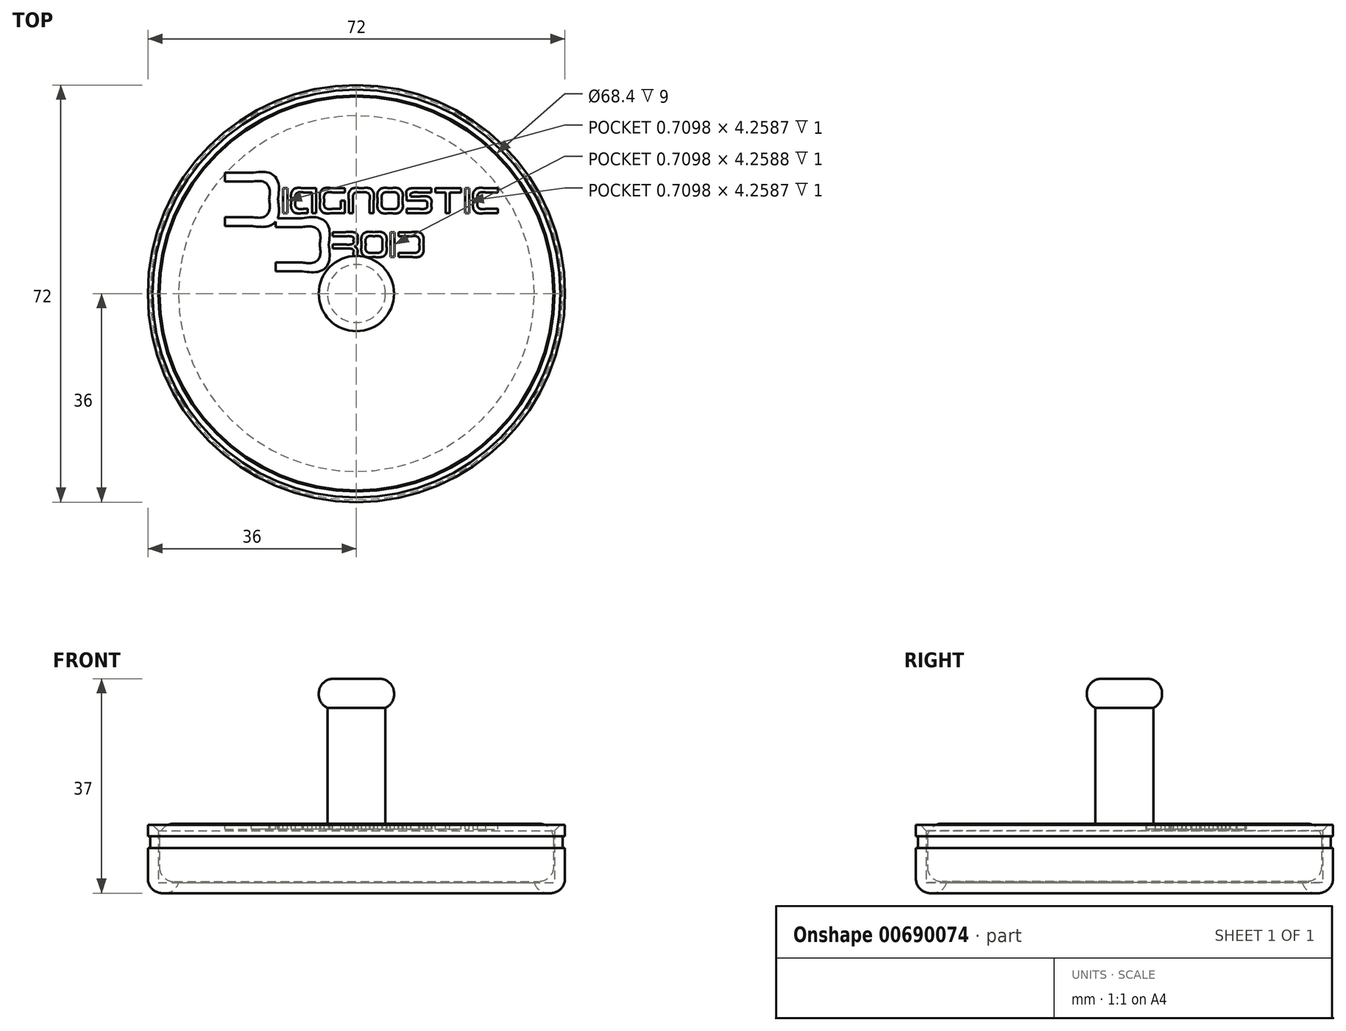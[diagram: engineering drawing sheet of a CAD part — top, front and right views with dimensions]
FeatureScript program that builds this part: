
annotation { "Feature Type Name" : "Feature", "Feature Type Description" : "" }
export const myFeature = defineFeature(function(context is Context, id is Id, definition is map)
    precondition{}
    {
        {
            var Q0;
            Q0=qCreatedBy(makeId("Front.planeOp"),FACE);
            var sketch = newSketch(context, id + "F0", { "sketchPlane" : qUnion([Q0])});
            skLineSegment(sketch, "E0.bottom", {"start": v(0, 0) * mm, "end": v(-34, 0) * mm});
            skLineSegment(sketch, "E0.top", {"start": v(0, 10) * mm, "end": v(-34, 10) * mm});
            skLineSegment(sketch, "E0.left", {"start": v(0, 0) * mm, "end": v(0, 10) * mm});
            skLineSegment(sketch, "E0.right", {"start": v(-34, 0) * mm, "end": v(-34, 6.5) * mm});
            skPoint(sketch, "E1.oppositeSnap0", {"position": v(-34, 5) * mm});
            skLineSegment(sketch, "E2.trimOffspring", {"start": v(-34, 3.5) * mm, "end": v(-34, 10) * mm});
            skLineSegment(sketch, "E3", {"start": v(-34, 6.5) * mm, "end": v(-34, 3.5) * mm});
            skPoint(sketch, "E1.top.end.orphan", {"position": v(-33.5, 6.5) * mm});
            skLineSegment(sketch, "E4.0", {"start": v(-36, -2) * mm, "end": v(-36, 9.8) * mm});
            skLineSegment(sketch, "E4.1", {"start": v(-30.7, -2) * mm, "end": v(-36, -2) * mm});
            skLineSegment(sketch, "E5.0", {"start": v(-34.2, -0.2) * mm, "end": v(-34.2, 9.8) * mm});
            skLineSegment(sketch, "E5.1", {"start": v(-30.7, -0.2) * mm, "end": v(-34.2, -0.2) * mm});
            skLineSegment(sketch, "E6", {"start": v(-34.2, 9.8) * mm, "end": v(-36, 9.8) * mm});
            skLineSegment(sketch, "E7", {"start": v(-30.7, -0.2) * mm, "end": v(-30.7, -2) * mm});
            skLineSegment(sketch, "E8.bottom", {"start": v(-36, 7.8) * mm, "end": v(-35.6, 7.8) * mm});
            skLineSegment(sketch, "E8.top", {"start": v(-36, 5.8) * mm, "end": v(-35.6, 5.8) * mm});
            skLineSegment(sketch, "E8.left", {"start": v(-36, 7.8) * mm, "end": v(-36, 5.8) * mm});
            skLineSegment(sketch, "E8.right", {"start": v(-35.6, 7.8) * mm, "end": v(-35.6, 5.8) * mm});
            skSolve(sketch);
        }
        {
            var Q0;
            Q0=makeQuery(id+"F0.imprint","IMPRINT",FACE,{"disambiguationData":[TD([[makeQuery(id+"F0.imprint","IMPRINT",EDGE,{"derivedFrom":sQuery(id+"F0.wireOp",EDGE,"E0.bottom")}),-1.0]])]});
            var Q1;
            Q1=makeQuery(id+"F0.imprint","IMPRINT",FACE,{"disambiguationData":[TD([[makeQuery(id+"F0.imprint","IMPRINT",EDGE,{"derivedFrom":sQuery(id+"F0.wireOp",EDGE,"E4.0")}),-1.0]])]});
            var Q2;
            Q2=sQuery(id+"F0.wireOp",EDGE,"E0.left");
            revolve(context, id + "F1", {"entities" : qUnion([Q0, Q1]), "axis" : qUnion([Q2]), "revolveType" : RevolveType.FULL});
        }
        {
            var Q0;
            Q0=makeQuery(id+"F1.opRevolve","SWEPT_FACE",FACE,{"disambiguationData":[OSD([sQuery(id+"F0.wireOp",EDGE,"E0.top")])]});
            var sketch = newSketch(context, id + "F2", { "sketchPlane" : qUnion([Q0])});
            skLineSegment(sketch, "E9", {"start": v(-11.94, 18.18) * mm, "end": v(-11.94, 13.92) * mm});
            skLineSegment(sketch, "E10", {"start": v(-11.94, 13.92) * mm, "end": v(-12.65, 13.92) * mm});
            skLineSegment(sketch, "E11", {"start": v(-12.65, 13.92) * mm, "end": v(-12.65, 18.18) * mm});
            skLineSegment(sketch, "E12", {"start": v(-12.65, 18.18) * mm, "end": v(-11.94, 18.18) * mm});
            skFitSpline(sketch, "E13", {"points": [v(-9.1, 17.47) * mm, v(-10.05, 17.47) * mm, v(-10.52, 17) * mm, v(-10.52, 16.05) * mm]});
            skFitSpline(sketch, "E14", {"points": [v(-10.52, 16.05) * mm, v(-10.52, 15.1) * mm, v(-10.05, 14.63) * mm, v(-9.1, 14.63) * mm]});
            skLineSegment(sketch, "E15", {"start": v(-6.97, 18.18) * mm, "end": v(-6.97, 13.92) * mm});
            skLineSegment(sketch, "E16", {"start": v(-6.97, 13.92) * mm, "end": v(-7.68, 13.92) * mm});
            skLineSegment(sketch, "E17", {"start": v(-7.68, 13.92) * mm, "end": v(-7.68, 17.47) * mm});
            skLineSegment(sketch, "E18", {"start": v(-7.68, 17.47) * mm, "end": v(-9.1, 17.47) * mm});
            skFitSpline(sketch, "E19", {"points": [v(-9.1, 13.92) * mm, v(-10.52, 13.92) * mm, v(-11.23, 14.63) * mm, v(-11.23, 16.05) * mm]});
            skFitSpline(sketch, "E20", {"points": [v(-11.23, 16.05) * mm, v(-11.23, 17.47) * mm, v(-10.52, 18.18) * mm, v(-9.1, 18.18) * mm]});
            skLineSegment(sketch, "E21", {"start": v(-9.1, 14.63) * mm, "end": v(-8.39, 14.63) * mm});
            skLineSegment(sketch, "E22", {"start": v(-8.39, 14.63) * mm, "end": v(-8.39, 13.92) * mm});
            skLineSegment(sketch, "E23", {"start": v(-8.39, 13.92) * mm, "end": v(-9.1, 13.92) * mm});
            skLineSegment(sketch, "E24", {"start": v(-9.1, 18.18) * mm, "end": v(-6.97, 18.18) * mm});
            skFitSpline(sketch, "E25", {"points": [v(-4.13, 13.92) * mm, v(-5.55, 13.92) * mm, v(-6.26, 14.63) * mm, v(-6.26, 16.05) * mm]});
            skFitSpline(sketch, "E26", {"points": [v(-6.26, 16.05) * mm, v(-6.26, 17.47) * mm, v(-5.55, 18.18) * mm, v(-4.13, 18.18) * mm]});
            skLineSegment(sketch, "E27", {"start": v(-2, 16.05) * mm, "end": v(-2, 13.92) * mm});
            skLineSegment(sketch, "E28", {"start": v(-2, 13.92) * mm, "end": v(-4.13, 13.92) * mm});
            skFitSpline(sketch, "E29", {"points": [v(-4.13, 17.47) * mm, v(-5.08, 17.47) * mm, v(-5.55, 17) * mm, v(-5.55, 16.05) * mm]});
            skFitSpline(sketch, "E30", {"points": [v(-5.55, 16.05) * mm, v(-5.55, 15.1) * mm, v(-5.08, 14.63) * mm, v(-4.13, 14.63) * mm]});
            skLineSegment(sketch, "E31", {"start": v(-4.13, 18.18) * mm, "end": v(-2, 18.18) * mm});
            skLineSegment(sketch, "E32", {"start": v(-2, 18.18) * mm, "end": v(-2, 17.47) * mm});
            skLineSegment(sketch, "E33", {"start": v(-2, 17.47) * mm, "end": v(-4.13, 17.47) * mm});
            skLineSegment(sketch, "E34", {"start": v(-4.13, 14.63) * mm, "end": v(-2.71, 14.63) * mm});
            skLineSegment(sketch, "E35", {"start": v(-2.71, 14.63) * mm, "end": v(-2.71, 16.05) * mm});
            skLineSegment(sketch, "E36", {"start": v(-2.71, 16.05) * mm, "end": v(-2, 16.05) * mm});
            skFitSpline(sketch, "E37", {"points": [v(-1.3, 16.05) * mm, v(-1.3, 17.47) * mm, v(-0.58, 18.18) * mm, v(0.84, 18.18) * mm]});
            skFitSpline(sketch, "E38", {"points": [v(0.84, 18.18) * mm, v(2.26, 18.18) * mm, v(2.97, 17.47) * mm, v(2.97, 16.05) * mm]});
            skLineSegment(sketch, "E39", {"start": v(-0.58, 16.05) * mm, "end": v(-0.58, 13.92) * mm});
            skLineSegment(sketch, "E40", {"start": v(-0.58, 13.92) * mm, "end": v(-1.3, 13.92) * mm});
            skLineSegment(sketch, "E41", {"start": v(-1.3, 13.92) * mm, "end": v(-1.3, 16.05) * mm});
            skFitSpline(sketch, "E42", {"points": [v(2.26, 16.05) * mm, v(2.26, 17) * mm, v(1.78, 17.47) * mm, v(0.84, 17.47) * mm]});
            skFitSpline(sketch, "E43", {"points": [v(0.84, 17.47) * mm, v(-0.1, 17.47) * mm, v(-0.58, 17) * mm, v(-0.58, 16.05) * mm]});
            skLineSegment(sketch, "E44", {"start": v(2.97, 16.05) * mm, "end": v(2.97, 13.92) * mm});
            skLineSegment(sketch, "E45", {"start": v(2.97, 13.92) * mm, "end": v(2.26, 13.92) * mm});
            skLineSegment(sketch, "E46", {"start": v(2.26, 13.92) * mm, "end": v(2.26, 16.05) * mm});
            skFitSpline(sketch, "E47", {"points": [v(3.68, 16.05) * mm, v(3.68, 17.47) * mm, v(4.39, 18.18) * mm, v(5.8, 18.18) * mm]});
            skFitSpline(sketch, "E48", {"points": [v(5.8, 18.18) * mm, v(7.23, 18.18) * mm, v(7.94, 17.47) * mm, v(7.94, 16.05) * mm]});
            skFitSpline(sketch, "E49", {"points": [v(7.94, 16.05) * mm, v(7.94, 14.63) * mm, v(7.23, 13.92) * mm, v(5.8, 13.92) * mm]});
            skFitSpline(sketch, "E50", {"points": [v(5.8, 13.92) * mm, v(4.39, 13.92) * mm, v(3.68, 14.63) * mm, v(3.68, 16.05) * mm]});
            skFitSpline(sketch, "E51", {"points": [v(4.39, 16.05) * mm, v(4.39, 15.1) * mm, v(4.86, 14.63) * mm, v(5.8, 14.63) * mm]});
            skFitSpline(sketch, "E52", {"points": [v(5.8, 14.63) * mm, v(6.75, 14.63) * mm, v(7.23, 15.1) * mm, v(7.23, 16.05) * mm]});
            skFitSpline(sketch, "E53", {"points": [v(7.23, 16.05) * mm, v(7.23, 17) * mm, v(6.75, 17.47) * mm, v(5.8, 17.47) * mm]});
            skFitSpline(sketch, "E54", {"points": [v(5.8, 17.47) * mm, v(4.86, 17.47) * mm, v(4.39, 17) * mm, v(4.39, 16.05) * mm]});
            skFitSpline(sketch, "E55", {"points": [v(8.65, 16.76) * mm, v(8.65, 17.7) * mm, v(9.36, 18.18) * mm, v(10.77, 18.18) * mm]});
            skFitSpline(sketch, "E56", {"points": [v(10.77, 17.47) * mm, v(9.83, 17.47) * mm, v(9.36, 17.23) * mm, v(9.36, 16.76) * mm]});
            skLineSegment(sketch, "E57", {"start": v(10.77, 18.18) * mm, "end": v(12.9, 18.18) * mm});
            skLineSegment(sketch, "E58", {"start": v(12.9, 18.18) * mm, "end": v(12.9, 17.47) * mm});
            skLineSegment(sketch, "E59", {"start": v(12.9, 17.47) * mm, "end": v(10.77, 17.47) * mm});
            skFitSpline(sketch, "E60", {"points": [v(10.77, 16.76) * mm, v(12.2, 16.76) * mm, v(12.9, 16.28) * mm, v(12.9, 15.34) * mm]});
            skFitSpline(sketch, "E61", {"points": [v(12.9, 15.34) * mm, v(12.9, 14.4) * mm, v(12.2, 13.92) * mm, v(10.77, 13.92) * mm]});
            skLineSegment(sketch, "E62", {"start": v(9.36, 16.76) * mm, "end": v(10.77, 16.76) * mm});
            skFitSpline(sketch, "E63", {"points": [v(10.77, 14.63) * mm, v(11.72, 14.63) * mm, v(12.2, 14.86) * mm, v(12.2, 15.34) * mm]});
            skFitSpline(sketch, "E64", {"points": [v(12.2, 15.34) * mm, v(12.2, 15.8) * mm, v(11.72, 16.05) * mm, v(10.77, 16.05) * mm]});
            skLineSegment(sketch, "E65", {"start": v(10.77, 13.92) * mm, "end": v(8.65, 13.92) * mm});
            skLineSegment(sketch, "E66", {"start": v(8.65, 13.92) * mm, "end": v(8.65, 14.63) * mm});
            skLineSegment(sketch, "E67", {"start": v(8.65, 14.63) * mm, "end": v(10.77, 14.63) * mm});
            skLineSegment(sketch, "E68", {"start": v(10.77, 16.05) * mm, "end": v(8.65, 16.05) * mm});
            skLineSegment(sketch, "E69", {"start": v(8.65, 16.05) * mm, "end": v(8.65, 16.76) * mm});
            skLineSegment(sketch, "E70", {"start": v(13.61, 18.18) * mm, "end": v(18.05, 18.18) * mm});
            skLineSegment(sketch, "E71", {"start": v(18.05, 18.18) * mm, "end": v(18.05, 17.47) * mm});
            skLineSegment(sketch, "E72", {"start": v(18.05, 17.47) * mm, "end": v(16.1, 17.47) * mm});
            skLineSegment(sketch, "E73", {"start": v(16.1, 17.47) * mm, "end": v(16.1, 13.92) * mm});
            skLineSegment(sketch, "E74", {"start": v(16.1, 13.92) * mm, "end": v(15.39, 13.92) * mm});
            skLineSegment(sketch, "E75", {"start": v(15.39, 13.92) * mm, "end": v(15.39, 17.47) * mm});
            skLineSegment(sketch, "E76", {"start": v(15.39, 17.47) * mm, "end": v(13.61, 17.47) * mm});
            skLineSegment(sketch, "E77", {"start": v(13.61, 17.47) * mm, "end": v(13.61, 18.18) * mm});
            skFitSpline(sketch, "E78", {"points": [v(20.9, 16.05) * mm, v(20.9, 15.1) * mm, v(21.37, 14.63) * mm, v(22.32, 14.63) * mm]});
            skLineSegment(sketch, "E79", {"start": v(19.48, 18.18) * mm, "end": v(19.48, 13.92) * mm});
            skLineSegment(sketch, "E80", {"start": v(19.48, 13.92) * mm, "end": v(18.77, 13.92) * mm});
            skLineSegment(sketch, "E81", {"start": v(18.77, 13.92) * mm, "end": v(18.77, 18.18) * mm});
            skLineSegment(sketch, "E82", {"start": v(18.77, 18.18) * mm, "end": v(19.48, 18.18) * mm});
            skFitSpline(sketch, "E83", {"points": [v(22.32, 13.92) * mm, v(20.9, 13.92) * mm, v(20.19, 14.63) * mm, v(20.19, 16.05) * mm]});
            skFitSpline(sketch, "E84", {"points": [v(20.19, 16.05) * mm, v(20.19, 17.47) * mm, v(20.9, 18.18) * mm, v(22.32, 18.18) * mm]});
            skLineSegment(sketch, "E85", {"start": v(22.32, 14.63) * mm, "end": v(24.45, 14.63) * mm});
            skLineSegment(sketch, "E86", {"start": v(24.45, 14.63) * mm, "end": v(24.45, 13.92) * mm});
            skLineSegment(sketch, "E87", {"start": v(24.45, 13.92) * mm, "end": v(22.32, 13.92) * mm});
            skFitSpline(sketch, "E88", {"points": [v(22.32, 17.47) * mm, v(21.37, 17.47) * mm, v(20.9, 17) * mm, v(20.9, 16.05) * mm]});
            skLineSegment(sketch, "E89", {"start": v(22.32, 18.18) * mm, "end": v(24.45, 18.18) * mm});
            skLineSegment(sketch, "E90", {"start": v(24.45, 18.18) * mm, "end": v(24.45, 17.47) * mm});
            skLineSegment(sketch, "E91", {"start": v(24.45, 17.47) * mm, "end": v(22.32, 17.47) * mm});
            skFitSpline(sketch, "E92", {"points": [v(-1.94, 8.47) * mm, v(-1, 8.47) * mm, v(-0.52, 8.71) * mm, v(-0.52, 9.18) * mm]});
            skFitSpline(sketch, "E93", {"points": [v(-0.52, 9.18) * mm, v(-0.52, 9.66) * mm, v(-1, 9.9) * mm, v(-1.94, 9.9) * mm]});
            skFitSpline(sketch, "E94", {"points": [v(-1.94, 10.6) * mm, v(-0.52, 10.6) * mm, v(0.19, 10.13) * mm, v(0.19, 9.18) * mm]});
            skFitSpline(sketch, "E95", {"points": [v(0.19, 9.18) * mm, v(0.19, 8.71) * mm, v(0.01, 8.36) * mm, v(-0.34, 8.12) * mm]});
            skFitSpline(sketch, "E96", {"points": [v(-0.34, 8.12) * mm, v(0.01, 7.88) * mm, v(0.19, 7.53) * mm, v(0.19, 7.05) * mm]});
            skLineSegment(sketch, "E97", {"start": v(-1.94, 9.9) * mm, "end": v(-4.07, 9.9) * mm});
            skLineSegment(sketch, "E98", {"start": v(-4.07, 9.9) * mm, "end": v(-4.07, 10.6) * mm});
            skLineSegment(sketch, "E99", {"start": v(-4.07, 10.6) * mm, "end": v(-1.94, 10.6) * mm});
            skFitSpline(sketch, "E100", {"points": [v(-0.52, 7.05) * mm, v(-0.52, 7.53) * mm, v(-1, 7.76) * mm, v(-1.94, 7.76) * mm]});
            skLineSegment(sketch, "E101", {"start": v(0.19, 7.05) * mm, "end": v(0.19, 6.34) * mm});
            skLineSegment(sketch, "E102", {"start": v(0.19, 6.34) * mm, "end": v(-0.52, 6.34) * mm});
            skLineSegment(sketch, "E103", {"start": v(-0.52, 6.34) * mm, "end": v(-0.52, 7.05) * mm});
            skFitSpline(sketch, "E104", {"points": [v(0.9, 8.47) * mm, v(0.9, 9.9) * mm, v(1.6, 10.6) * mm, v(3.03, 10.6) * mm]});
            skFitSpline(sketch, "E105", {"points": [v(3.03, 10.6) * mm, v(4.45, 10.6) * mm, v(5.16, 9.9) * mm, v(5.16, 8.47) * mm]});
            skFitSpline(sketch, "E106", {"points": [v(5.16, 8.47) * mm, v(5.16, 7.05) * mm, v(4.45, 6.34) * mm, v(3.03, 6.34) * mm]});
            skFitSpline(sketch, "E107", {"points": [v(3.03, 6.34) * mm, v(1.6, 6.34) * mm, v(0.9, 7.05) * mm, v(0.9, 8.47) * mm]});
            skLineSegment(sketch, "E108", {"start": v(-1.94, 7.76) * mm, "end": v(-4.07, 7.76) * mm});
            skLineSegment(sketch, "E109", {"start": v(-4.07, 7.76) * mm, "end": v(-4.07, 8.47) * mm});
            skLineSegment(sketch, "E110", {"start": v(-4.07, 8.47) * mm, "end": v(-1.94, 8.47) * mm});
            skFitSpline(sketch, "E111", {"points": [v(1.6, 8.47) * mm, v(1.6, 7.53) * mm, v(2.08, 7.05) * mm, v(3.03, 7.05) * mm]});
            skFitSpline(sketch, "E112", {"points": [v(3.03, 7.05) * mm, v(3.97, 7.05) * mm, v(4.45, 7.53) * mm, v(4.45, 8.47) * mm]});
            skFitSpline(sketch, "E113", {"points": [v(4.45, 8.47) * mm, v(4.45, 9.42) * mm, v(3.97, 9.9) * mm, v(3.03, 9.9) * mm]});
            skFitSpline(sketch, "E114", {"points": [v(3.03, 9.9) * mm, v(2.08, 9.9) * mm, v(1.6, 9.42) * mm, v(1.6, 8.47) * mm]});
            skLineSegment(sketch, "E115", {"start": v(6.58, 10.6) * mm, "end": v(6.58, 6.34) * mm});
            skLineSegment(sketch, "E116", {"start": v(6.58, 6.34) * mm, "end": v(5.87, 6.34) * mm});
            skLineSegment(sketch, "E117", {"start": v(5.87, 6.34) * mm, "end": v(5.87, 10.6) * mm});
            skLineSegment(sketch, "E118", {"start": v(5.87, 10.6) * mm, "end": v(6.58, 10.6) * mm});
            skFitSpline(sketch, "E119", {"points": [v(9.41, 10.6) * mm, v(10.83, 10.6) * mm, v(11.54, 9.9) * mm, v(11.54, 8.47) * mm]});
            skFitSpline(sketch, "E120", {"points": [v(11.54, 8.47) * mm, v(11.54, 7.05) * mm, v(10.83, 6.34) * mm, v(9.41, 6.34) * mm]});
            skLineSegment(sketch, "E121", {"start": v(9.41, 9.9) * mm, "end": v(7.29, 9.9) * mm});
            skLineSegment(sketch, "E122", {"start": v(7.29, 9.9) * mm, "end": v(7.29, 10.6) * mm});
            skLineSegment(sketch, "E123", {"start": v(7.29, 10.6) * mm, "end": v(9.41, 10.6) * mm});
            skFitSpline(sketch, "E124", {"points": [v(9.41, 7.05) * mm, v(10.36, 7.05) * mm, v(10.83, 7.53) * mm, v(10.83, 8.47) * mm]});
            skFitSpline(sketch, "E125", {"points": [v(10.83, 8.47) * mm, v(10.83, 9.42) * mm, v(10.36, 9.9) * mm, v(9.41, 9.9) * mm]});
            skLineSegment(sketch, "E126", {"start": v(9.41, 6.34) * mm, "end": v(7.29, 6.34) * mm});
            skLineSegment(sketch, "E127", {"start": v(7.29, 6.34) * mm, "end": v(7.29, 7.05) * mm});
            skLineSegment(sketch, "E128", {"start": v(7.29, 7.05) * mm, "end": v(9.41, 7.05) * mm});
            skFitSpline(sketch, "E129", {"points": [v(-18.13, 20.85) * mm, v(-15.07, 20.85) * mm, v(-13.54, 19.32) * mm, v(-13.54, 16.26) * mm]});
            skFitSpline(sketch, "E130", {"points": [v(-13.54, 16.26) * mm, v(-13.54, 13.2) * mm, v(-15.07, 11.67) * mm, v(-18.13, 11.67) * mm]});
            skLineSegment(sketch, "E131", {"start": v(-18.13, 19.32) * mm, "end": v(-22.71, 19.32) * mm});
            skLineSegment(sketch, "E132", {"start": v(-22.71, 19.32) * mm, "end": v(-22.71, 20.85) * mm});
            skLineSegment(sketch, "E133", {"start": v(-22.71, 20.85) * mm, "end": v(-18.13, 20.85) * mm});
            skFitSpline(sketch, "E134", {"points": [v(-18.13, 13.2) * mm, v(-16.1, 13.2) * mm, v(-15.07, 14.22) * mm, v(-15.07, 16.26) * mm]});
            skFitSpline(sketch, "E135", {"points": [v(-15.07, 16.26) * mm, v(-15.07, 18.3) * mm, v(-16.1, 19.32) * mm, v(-18.13, 19.32) * mm]});
            skLineSegment(sketch, "E136", {"start": v(-18.13, 11.67) * mm, "end": v(-22.71, 11.67) * mm});
            skLineSegment(sketch, "E137", {"start": v(-22.71, 11.67) * mm, "end": v(-22.71, 13.2) * mm});
            skLineSegment(sketch, "E138", {"start": v(-22.71, 13.2) * mm, "end": v(-18.13, 13.2) * mm});
            skFitSpline(sketch, "E139", {"points": [v(-9.38, 13.02) * mm, v(-6.32, 13.02) * mm, v(-4.8, 11.49) * mm, v(-4.8, 8.43) * mm]});
            skFitSpline(sketch, "E140", {"points": [v(-4.8, 8.43) * mm, v(-4.8, 5.37) * mm, v(-6.32, 3.85) * mm, v(-9.38, 3.85) * mm]});
            skLineSegment(sketch, "E141", {"start": v(-9.38, 11.49) * mm, "end": v(-13.97, 11.49) * mm});
            skLineSegment(sketch, "E142", {"start": v(-13.97, 11.49) * mm, "end": v(-13.97, 13.02) * mm});
            skLineSegment(sketch, "E143", {"start": v(-13.97, 13.02) * mm, "end": v(-9.38, 13.02) * mm});
            skFitSpline(sketch, "E144", {"points": [v(-9.38, 5.37) * mm, v(-7.34, 5.37) * mm, v(-6.32, 6.4) * mm, v(-6.32, 8.43) * mm]});
            skFitSpline(sketch, "E145", {"points": [v(-6.32, 8.43) * mm, v(-6.32, 10.47) * mm, v(-7.34, 11.49) * mm, v(-9.38, 11.49) * mm]});
            skLineSegment(sketch, "E146", {"start": v(-9.04, 3.85) * mm, "end": v(-13.97, 3.85) * mm});
            skLineSegment(sketch, "E147", {"start": v(-13.97, 5.37) * mm, "end": v(-9.04, 5.37) * mm});
            skLineSegment(sketch, "E148", {"start": v(-13.97, 5.37) * mm, "end": v(-13.97, 3.85) * mm});
            skSolve(sketch);
        }
        {
            var Q0;
            Q0=makeQuery(id+"F2.imprint","IMPRINT",FACE,{"disambiguationData":[TD([[makeQuery(id+"F2.imprint","IMPRINT",EDGE,{"derivedFrom":sQuery(id+"F2.wireOp",EDGE,"E111")}),1.0]])]});
            var Q1;
            Q1=makeQuery(id+"F2.imprint","IMPRINT",FACE,{"disambiguationData":[TD([[makeQuery(id+"F2.imprint","IMPRINT",EDGE,{"derivedFrom":sQuery(id+"F2.wireOp",EDGE,"E9")}),1.0]])]});
            var Q2;
            Q2=sQuery(id+"F2.wireOp",EDGE,"E99");
            var Q3;
            Q3=sQuery(id+"F2.wireOp",EDGE,"E115");
            var Q4;
            Q4=sQuery(id+"F2.wireOp",EDGE,"E131");
            var Q5;
            Q5=sQuery(id+"F2.wireOp",EDGE,"E147");
            var Q6;
            Q6=sQuery(id+"F2.wireOp",EDGE,"E51");
            var Q7;
            Q7=sQuery(id+"F2.wireOp",EDGE,"E67");
            var Q8;
            Q8=sQuery(id+"F2.wireOp",EDGE,"E83");
            var Q9;
            Q9=sQuery(id+"F2.wireOp",EDGE,"E114");
            var Q10;
            Q10=sQuery(id+"F2.wireOp",EDGE,"E130");
            var Q11;
            Q11=sQuery(id+"F2.wireOp",EDGE,"E146");
            var Q12;
            Q12=sQuery(id+"F2.wireOp",EDGE,"E50");
            var Q13;
            Q13=sQuery(id+"F2.wireOp",EDGE,"E20");
            var Q14;
            Q14=sQuery(id+"F2.wireOp",EDGE,"E19");
            var Q15;
            Q15=sQuery(id+"F2.wireOp",EDGE,"E17");
            var Q16;
            Q16=sQuery(id+"F2.wireOp",EDGE,"E15");
            var Q17;
            Q17=sQuery(id+"F2.wireOp",EDGE,"E14");
            var Q18;
            Q18=sQuery(id+"F2.wireOp",EDGE,"E13");
            var Q19;
            Q19=sQuery(id+"F2.wireOp",EDGE,"E11");
            var Q20;
            Q20=sQuery(id+"F2.wireOp",EDGE,"E9");
            var Q21;
            Q21=sQuery(id+"F2.wireOp",EDGE,"E97");
            var Q22;
            Q22=sQuery(id+"F2.wireOp",EDGE,"E113");
            var Q23;
            Q23=sQuery(id+"F2.wireOp",EDGE,"E129");
            var Q24;
            Q24=sQuery(id+"F2.wireOp",EDGE,"E145");
            var Q25;
            Q25=sQuery(id+"F2.wireOp",EDGE,"E33");
            var Q26;
            Q26=sQuery(id+"F2.wireOp",EDGE,"E49");
            var Q27;
            Q27=sQuery(id+"F2.wireOp",EDGE,"E65");
            var Q28;
            Q28=sQuery(id+"F2.wireOp",EDGE,"E81");
            var Q29;
            Q29=sQuery(id+"F2.wireOp",EDGE,"E112");
            var Q30;
            Q30=sQuery(id+"F2.wireOp",EDGE,"E128");
            var Q31;
            Q31=sQuery(id+"F2.wireOp",EDGE,"E144");
            var Q32;
            Q32=sQuery(id+"F2.wireOp",EDGE,"E48");
            var Q33;
            Q33=sQuery(id+"F2.wireOp",EDGE,"E143");
            var Q34;
            Q34=sQuery(id+"F2.wireOp",EDGE,"E79");
            var Q35;
            Q35=sQuery(id+"F2.wireOp",EDGE,"E111");
            var Q36;
            Q36=sQuery(id+"F2.wireOp",EDGE,"E31");
            var Q37;
            Q37=sQuery(id+"F2.wireOp",EDGE,"E47");
            var Q38;
            Q38=sQuery(id+"F2.wireOp",EDGE,"E126");
            var Q39;
            Q39=sQuery(id+"F2.wireOp",EDGE,"E78");
            var Q40;
            Q40=sQuery(id+"F2.wireOp",EDGE,"E94");
            var Q41;
            Q41=sQuery(id+"F2.wireOp",EDGE,"E110");
            var Q42;
            Q42=sQuery(id+"F2.wireOp",EDGE,"E125");
            var Q43;
            Q43=sQuery(id+"F2.wireOp",EDGE,"E141");
            var Q44;
            Q44=sQuery(id+"F2.wireOp",EDGE,"E61");
            var Q45;
            Q45=sQuery(id+"F2.wireOp",EDGE,"E29");
            var Q46;
            Q46=sQuery(id+"F2.wireOp",EDGE,"E124");
            var Q47;
            Q47=sQuery(id+"F2.wireOp",EDGE,"E140");
            var Q48;
            Q48=sQuery(id+"F2.wireOp",EDGE,"E60");
            var Q49;
            Q49=sQuery(id+"F2.wireOp",EDGE,"E108");
            var Q50;
            Q50=sQuery(id+"F2.wireOp",EDGE,"E123");
            var Q51;
            Q51=sQuery(id+"F2.wireOp",EDGE,"E139");
            var Q52;
            Q52=sQuery(id+"F2.wireOp",EDGE,"E59");
            var Q53;
            Q53=sQuery(id+"F2.wireOp",EDGE,"E75");
            var Q54;
            Q54=sQuery(id+"F2.wireOp",EDGE,"E91");
            var Q55;
            Q55=sQuery(id+"F2.wireOp",EDGE,"E107");
            var Q56;
            Q56=sQuery(id+"F2.wireOp",EDGE,"E43");
            var Q57;
            Q57=sQuery(id+"F2.wireOp",EDGE,"E106");
            var Q58;
            Q58=sQuery(id+"F2.wireOp",EDGE,"E26");
            var Q59;
            Q59=sQuery(id+"F2.wireOp",EDGE,"E42");
            var Q60;
            Q60=sQuery(id+"F2.wireOp",EDGE,"E138");
            var Q61;
            Q61=sQuery(id+"F2.wireOp",EDGE,"E25");
            var Q62;
            Q62=sQuery(id+"F2.wireOp",EDGE,"E121");
            var Q63;
            Q63=sQuery(id+"F2.wireOp",EDGE,"E57");
            var Q64;
            Q64=sQuery(id+"F2.wireOp",EDGE,"E73");
            var Q65;
            Q65=sQuery(id+"F2.wireOp",EDGE,"E89");
            var Q66;
            Q66=sQuery(id+"F2.wireOp",EDGE,"E105");
            var Q67;
            Q67=sQuery(id+"F2.wireOp",EDGE,"E120");
            var Q68;
            Q68=sQuery(id+"F2.wireOp",EDGE,"E88");
            var Q69;
            Q69=sQuery(id+"F2.wireOp",EDGE,"E104");
            var Q70;
            Q70=sQuery(id+"F2.wireOp",EDGE,"E119");
            var Q71;
            Q71=sQuery(id+"F2.wireOp",EDGE,"E135");
            var Q72;
            Q72=sQuery(id+"F2.wireOp",EDGE,"E55");
            var Q73;
            Q73=sQuery(id+"F2.wireOp",EDGE,"E87");
            var Q74;
            Q74=sQuery(id+"F2.wireOp",EDGE,"E117");
            var Q75;
            Q75=sQuery(id+"F2.wireOp",EDGE,"E133");
            var Q76;
            Q76=sQuery(id+"F2.wireOp",EDGE,"E37");
            var Q77;
            Q77=sQuery(id+"F2.wireOp",EDGE,"E53");
            var Q78;
            Q78=sQuery(id+"F2.wireOp",EDGE,"E85");
            var Q79;
            Q79=sQuery(id+"F2.wireOp",EDGE,"E134");
            var Q80;
            Q80=sQuery(id+"F2.wireOp",EDGE,"E54");
            var Q81;
            Q81=sQuery(id+"F2.wireOp",EDGE,"E38");
            var Q82;
            Q82=sQuery(id+"F2.wireOp",EDGE,"E52");
            var Q83;
            Q83=sQuery(id+"F2.wireOp",EDGE,"E68");
            var Q84;
            Q84=sQuery(id+"F2.wireOp",EDGE,"E84");
            var Q85;
            Q85=sQuery(id+"F2.wireOp",EDGE,"E35");
            var Q86;
            Q86=sQuery(id+"F2.wireOp",EDGE,"E34");
            var Q87;
            Q87=sQuery(id+"F2.wireOp",EDGE,"E66");
            var Q88;
            Q88=sQuery(id+"F2.wireOp",EDGE,"E82");
            var Q89;
            Q89=sQuery(id+"F2.wireOp",EDGE,"E18");
            var Q90;
            Q90=sQuery(id+"F2.wireOp",EDGE,"E12");
            var Q91;
            Q91=sQuery(id+"F2.wireOp",EDGE,"E10");
            var Q92;
            Q92=sQuery(id+"F2.wireOp",EDGE,"E24");
            var Q93;
            Q93=sQuery(id+"F2.wireOp",EDGE,"E96");
            var Q94;
            Q94=sQuery(id+"F2.wireOp",EDGE,"E32");
            var Q95;
            Q95=sQuery(id+"F2.wireOp",EDGE,"E64");
            var Q96;
            Q96=sQuery(id+"F2.wireOp",EDGE,"E80");
            var Q97;
            Q97=sQuery(id+"F2.wireOp",EDGE,"E127");
            var Q98;
            Q98=sQuery(id+"F2.wireOp",EDGE,"E63");
            var Q99;
            Q99=sQuery(id+"F2.wireOp",EDGE,"E95");
            var Q100;
            Q100=sQuery(id+"F2.wireOp",EDGE,"E142");
            var Q101;
            Q101=sQuery(id+"F2.wireOp",EDGE,"E62");
            var Q102;
            Q102=sQuery(id+"F2.wireOp",EDGE,"E30");
            var Q103;
            Q103=sQuery(id+"F2.wireOp",EDGE,"E46");
            var Q104;
            Q104=sQuery(id+"F2.wireOp",EDGE,"E77");
            var Q105;
            Q105=sQuery(id+"F2.wireOp",EDGE,"E93");
            var Q106;
            Q106=sQuery(id+"F2.wireOp",EDGE,"E109");
            var Q107;
            Q107=sQuery(id+"F2.wireOp",EDGE,"E45");
            var Q108;
            Q108=sQuery(id+"F2.wireOp",EDGE,"E76");
            var Q109;
            Q109=sQuery(id+"F2.wireOp",EDGE,"E92");
            var Q110;
            Q110=sQuery(id+"F2.wireOp",EDGE,"E28");
            var Q111;
            Q111=sQuery(id+"F2.wireOp",EDGE,"E44");
            var Q112;
            Q112=sQuery(id+"F2.wireOp",EDGE,"E27");
            var Q113;
            Q113=sQuery(id+"F2.wireOp",EDGE,"E58");
            var Q114;
            Q114=sQuery(id+"F2.wireOp",EDGE,"E74");
            var Q115;
            Q115=sQuery(id+"F2.wireOp",EDGE,"E90");
            var Q116;
            Q116=sQuery(id+"F2.wireOp",EDGE,"E41");
            var Q117;
            Q117=sQuery(id+"F2.wireOp",EDGE,"E137");
            var Q118;
            Q118=sQuery(id+"F2.wireOp",EDGE,"E56");
            var Q119;
            Q119=sQuery(id+"F2.wireOp",EDGE,"E72");
            var Q120;
            Q120=sQuery(id+"F2.wireOp",EDGE,"E71");
            var Q121;
            Q121=sQuery(id+"F2.wireOp",EDGE,"E103");
            var Q122;
            Q122=sQuery(id+"F2.wireOp",EDGE,"E39");
            var Q123;
            Q123=sQuery(id+"F2.wireOp",EDGE,"E101");
            var Q124;
            Q124=sQuery(id+"F2.wireOp",EDGE,"E70");
            var Q125;
            Q125=sQuery(id+"F2.wireOp",EDGE,"E86");
            var Q126;
            Q126=sQuery(id+"F2.wireOp",EDGE,"E102");
            var Q127;
            Q127=sQuery(id+"F2.wireOp",EDGE,"E100");
            var Q128;
            Q128=sQuery(id+"F2.wireOp",EDGE,"E116");
            var Q129;
            Q129=sQuery(id+"F2.wireOp",EDGE,"E132");
            var Q130;
            Q130=sQuery(id+"F2.wireOp",EDGE,"E148");
            var Q131;
            Q131=sQuery(id+"F2.wireOp",EDGE,"E36");
            var Q132;
            Q132=sQuery(id+"F2.wireOp",EDGE,"E16");
            var Q133;
            Q133=sQuery(id+"F2.wireOp",EDGE,"E122");
            var Q134;
            Q134=sQuery(id+"F2.wireOp",EDGE,"E40");
            var Q135;
            Q135=sQuery(id+"F2.wireOp",EDGE,"E118");
            var Q136;
            Q136=sQuery(id+"F2.wireOp",EDGE,"E98");
            var Q137;
            Q137=sQuery(id+"F2.wireOp",EDGE,"E21");
            var Q138;
            Q138=sQuery(id+"F2.wireOp",EDGE,"E23");
            var Q139;
            Q139=sQuery(id+"F2.wireOp",EDGE,"E22");
            var Q140;
            Q140=sQuery(id+"F2.wireOp",EDGE,"E69");
            var Q141;
            Q141=sQuery(id+"F2.wireOp",EDGE,"E136");
            extrude(context, id + "F3", {"entities" : qUnion([Q0, Q1]), "operationType" : NewBodyOperationType.REMOVE, "surfaceEntities" : qUnion([Q2, Q3, Q4, Q5, Q6, Q7, Q8, Q9, Q10, Q11, Q12, Q13, Q14, Q15, Q16, Q17, Q18, Q19, Q20, Q21, Q22, Q23, Q24, Q25, Q26, Q27, Q28, Q29, Q30, Q31, Q32, Q33, Q34, Q35, Q36, Q37, Q38, Q39, Q40, Q41, Q42, Q43, Q44, Q45, Q46, Q47, Q48, Q49, Q50, Q51, Q52, Q53, Q54, Q55, Q56, Q57, Q58, Q59, Q60, Q61, Q62, Q63, Q64, Q65, Q66, Q67, Q68, Q69, Q70, Q71, Q72, Q73, Q74, Q75, Q76, Q77, Q78, Q79, Q80, Q81, Q82, Q83, Q84, Q85, Q86, Q87, Q88, Q89, Q90, Q91, Q92, Q93, Q94, Q95, Q96, Q97, Q98, Q99, Q100, Q101, Q102, Q103, Q104, Q105, Q106, Q107, Q108, Q109, Q110, Q111, Q112, Q113, Q114, Q115, Q116, Q117, Q118, Q119, Q120, Q121, Q122, Q123, Q124, Q125, Q126, Q127, Q128, Q129, Q130, Q131, Q132, Q133, Q134, Q135, Q136, Q137, Q138, Q139, Q140, Q141]), "depth" : 1.5 * mm, "offsetDistance" : 25 * mm});
        }
        {
            var Q0;
            Q0=qSketchRegion(id+"F2",true);
            extrude(context, id + "F4", {"entities" : qUnion([Q0]), "operationType" : NewBodyOperationType.REMOVE, "oppositeDirection" : true, "depth" : 1 * mm, "offsetDistance" : 25 * mm});
        }
        {
            var Q0;
            Q0=makeQuery(id+"F1.opRevolve","SWEPT_EDGE",EDGE,{"disambiguationData":[OSD([sQuery(id+"F0.wireOp",EDGE,"E0.top"),sQuery(id+"F0.wireOp",EDGE,"E2.trimOffspring")])]});
            var Q1;
            Q1=makeQuery(id+"F1.opRevolve","SWEPT_EDGE",EDGE,{"disambiguationData":[OSD([sQuery(id+"F0.wireOp",EDGE,"E0.bottom"),sQuery(id+"F0.wireOp",EDGE,"E0.right")])]});
            var Q2;
            Q2=makeQuery(id+"F1.opRevolve","SWEPT_EDGE",EDGE,{"disambiguationData":[OSD([sQuery(id+"F0.wireOp",EDGE,"E4.0"),sQuery(id+"F0.wireOp",EDGE,"E4.1")])]});
            var Q3;
            Q3=makeQuery(id+"F1.opRevolve","SWEPT_EDGE",EDGE,{"disambiguationData":[OSD([sQuery(id+"F0.wireOp",EDGE,"E4.1"),sQuery(id+"F0.wireOp",EDGE,"E7")])]});
            fillet(context, id + "F5", {"entities" : qUnion([Q0, Q1, Q2, Q3]), "radius" : 2.5 * mm, "tangentPropagation" : true, "allowEdgeOverflow" : false});
        }
        {
            var Q0;
            Q0=makeQuery(id+"F1.opRevolve","SWEPT_EDGE",EDGE,{"disambiguationData":[OSD([sQuery(id+"F0.wireOp",EDGE,"E5.0"),sQuery(id+"F0.wireOp",EDGE,"E6")])]});
            var Q1;
            Q1=makeQuery(id+"F1.opRevolve","SWEPT_EDGE",EDGE,{"disambiguationData":[OSD([sQuery(id+"F0.wireOp",EDGE,"E4.1"),sQuery(id+"F0.wireOp",EDGE,"E7")])]});
            chamfer(context, id + "F6", {"entities" : qUnion([Q0, Q1]), "width" : 1 * mm, "tangentPropagation" : true});
        }
        {
            var Q0;
            Q0=makeQuery(id+"F1.opRevolve","SWEPT_FACE",FACE,{"disambiguationData":[OSD([sQuery(id+"F0.wireOp",EDGE,"E0.bottom")])]});
            var sketch = newSketch(context, id + "F7", { "sketchPlane" : qUnion([Q0])});
            skCircle(sketch, "E149", {"center": v(0, 0) * mm, "radius": 5 * mm});
            skSolve(sketch);
        }
        {
            var Q0;
            Q0=makeQuery(id+"F7.imprint","IMPRINT",FACE,{"disambiguationData":[TD([[makeQuery(id+"F7.imprint","IMPRINT",EDGE,{"derivedFrom":sQuery(id+"F7.wireOp",EDGE,"E149")}),1.0]])]});
            extrude(context, id + "F8", {"entities" : qUnion([Q0]), "operationType" : NewBodyOperationType.ADD, "oppositeDirection" : true, "depth" : 30 * mm, "offsetDistance" : 25 * mm});
        }
        {
            var Q0;
            Q0=makeQuery(id+"F8.opExtrude","CAP_FACE",FACE,{"disambiguationData":[OSD([sQuery(id+"F7.wireOp",EDGE,"E149")])],"isStart":false});
            var sketch = newSketch(context, id + "F9", { "sketchPlane" : qUnion([Q0])});
            skCircle(sketch, "E150", {"center": v(0, 0) * mm, "radius": 6.5 * mm});
            skSolve(sketch);
        }
        {
            var Q0;
            Q0=makeQuery(id+"F9.imprint","IMPRINT",FACE,{"disambiguationData":[TD([[makeQuery(id+"F9.imprint","IMPRINT",EDGE,{"derivedFrom":sQuery(id+"F9.wireOp",EDGE,"E150")}),1.0]])]});
            var Q1;
            Q1=makeQuery(id+"F9.imprint","IMPRINT",FACE,{"disambiguationData":[TD([[makeQuery(id+"F9.imprint","IMPRINT",EDGE,{"derivedFrom":makeQuery(id+"F8.opExtrude","CAP_EDGE",EDGE,{"disambiguationData":[OSD([sQuery(id+"F7.wireOp",EDGE,"E149")])],"isStart":false})}),-1.0]])]});
            extrude(context, id + "F10", {"entities" : qUnion([Q0, Q1]), "operationType" : NewBodyOperationType.ADD, "depth" : 5 * mm, "offsetDistance" : 25 * mm});
        }
        {
            var Q0;
            Q0=makeQuery(id+"F10.opExtrude","CAP_EDGE",EDGE,{"disambiguationData":[OSD([sQuery(id+"F9.wireOp",EDGE,"E150")])],"isStart":true});
            var Q1;
            Q1=makeQuery(id+"F10.opExtrude","CAP_EDGE",EDGE,{"disambiguationData":[OSD([sQuery(id+"F9.wireOp",EDGE,"E150")])],"isStart":false});
            fillet(context, id + "F11", {"entities" : qUnion([Q0, Q1]), "radius" : 2.5 * mm, "tangentPropagation" : true, "allowEdgeOverflow" : false});
        }
    });
